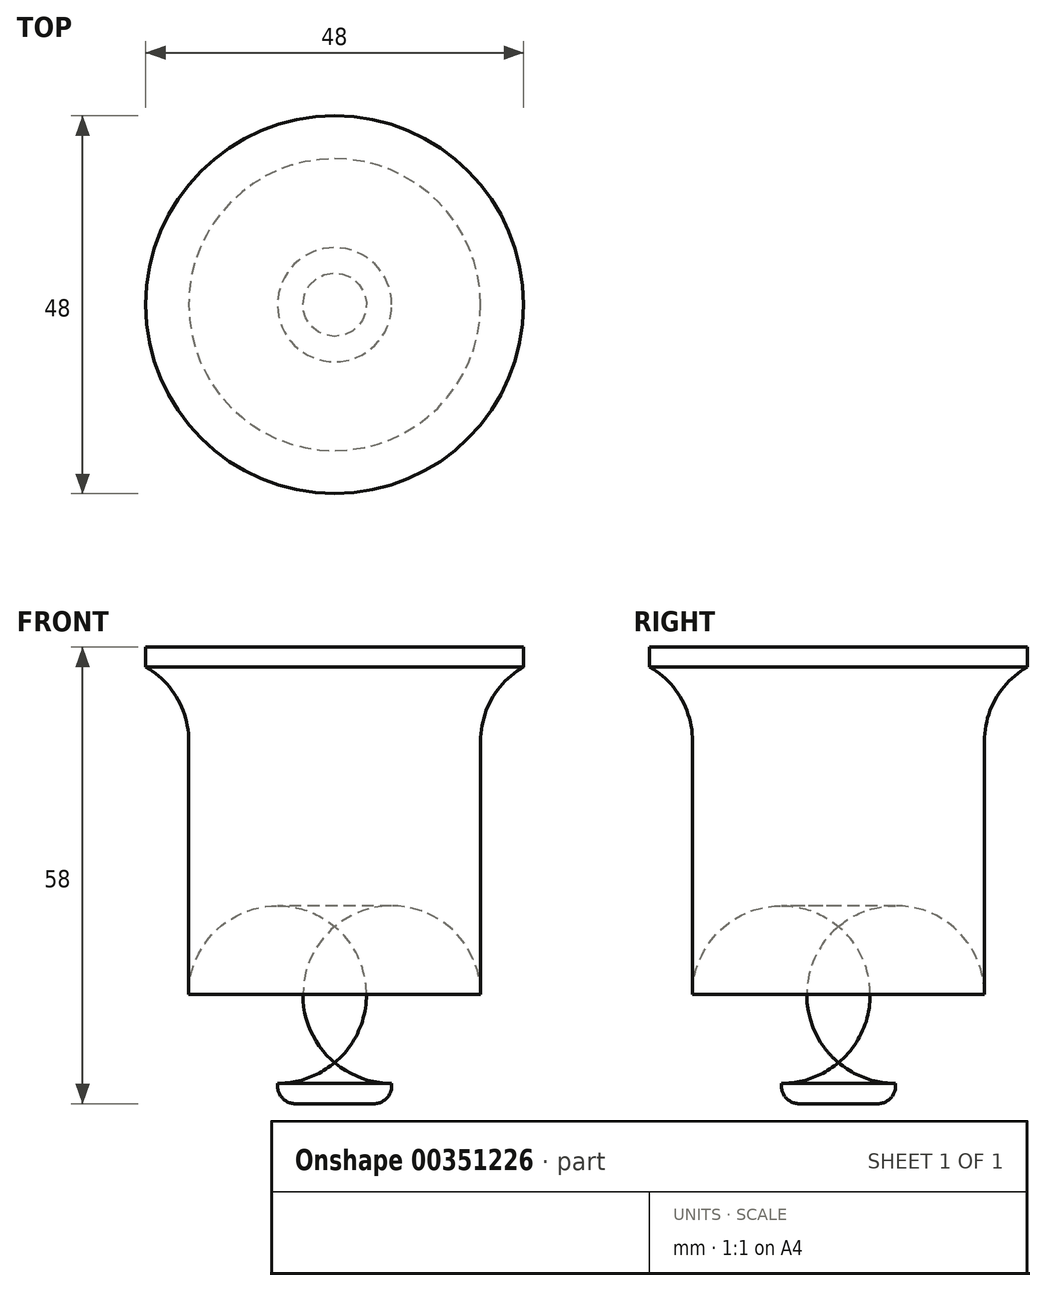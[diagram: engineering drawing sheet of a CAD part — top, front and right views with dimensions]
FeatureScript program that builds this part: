
annotation { "Feature Type Name" : "Feature", "Feature Type Description" : "" }
export const myFeature = defineFeature(function(context is Context, id is Id, definition is map)
    precondition{}
    {
        {
            var Q0;
            Q0=qCreatedBy(makeId("Front.planeOp"),FACE);
            var sketch = newSketch(context, id + "F0", { "sketchPlane" : qUnion([Q0])});
            skLineSegment(sketch, "E0", {"start": v(0, 0) * mm, "end": v(0, -58) * mm});
            skLineSegment(sketch, "E1", {"start": v(0, -58) * mm, "end": v(5, -58) * mm});
            skLineSegment(sketch, "E2", {"start": v(7.25, -55.74) * mm, "end": v(7.25, -55.43) * mm});
            skLineSegment(sketch, "E3", {"start": v(18.54, -44.14) * mm, "end": v(18.54, -11.96) * mm});
            skLineSegment(sketch, "E4", {"start": v(24, -2.5) * mm, "end": v(24, 0) * mm});
            skLineSegment(sketch, "E5", {"start": v(24, 0) * mm, "end": v(0, 0) * mm});
            skArc(sketch, "E6.filletArc", {"start": v(24, -2.5) * mm, "mid": v(20, -6.5) * mm, "end": v(18.54, -11.96) * mm});
            skPoint(sketch, "E7.visualSharp", {"position": v(18.54, -50.78) * mm});
            skArc(sketch, "E7.filletArc", {"start": v(7.25, -55.43) * mm, "mid": v(15.23, -52.12) * mm, "end": v(18.54, -44.14) * mm});
            skPoint(sketch, "E8.visualSharp", {"position": v(7.25, -58) * mm});
            skArc(sketch, "E8.filletArc", {"start": v(5, -58) * mm, "mid": v(6.6, -57.34) * mm, "end": v(7.25, -55.74) * mm});
            skLineSegment(sketch, "E9", {"start": v(29.46, -11.96) * mm, "end": v(24, -2.5) * mm, "construction": true});
            skSolve(sketch);
        }
        {
            var Q0;
            Q0=makeQuery(id+"F0.imprint","IMPRINT",FACE,{"disambiguationData":[TD([[makeQuery(id+"F0.imprint","IMPRINT",EDGE,{"derivedFrom":sQuery(id+"F0.wireOp",EDGE,"E0")}),1.0]])]});
            var Q1;
            Q1=sQuery(id+"F0.wireOp",EDGE,"E0");
            revolve(context, id + "F1", {"entities" : qUnion([Q0]), "axis" : qUnion([Q1]), "revolveType" : RevolveType.FULL});
        }
    });
